# Revit family: Haworth_Circa_Pendant
name_source: partatom
category: Lighting Fixtures
revit_build: Autodesk Revit 2018 (Build: 20170223_1515(x64)
units: mm (PartAtom-declared; Revit-internal decimal feet)

## family parameters
Always vertical = Yes
Cut with Voids When Loaded = No
Host = Ceiling
Light Source = Yes
OmniClass Number = 23.80.70.11
OmniClass Title = Luminaries for Internal Lighting
Part Type = Normal
Room Calculation Point = No
Round Connector Dimension = Use Diameter
Shared = No

## types (2) — shared parameters
Apparent Load = 0 VA
Assembly Code = D5020200
Color Filter = 16777215
Cords Finish = Haworth _ Metal _ Satin Aluminum_Grey-Cord TR-E05
Dimming Lamp Color Temperature Shift = <None>
Emit Shape Visible in Rendering = No
Emit from Circle Diameter = 1' - 6"
Glass Finish = Haworth _ Glass _ Frosted
Manufacturer = Haworth
Max. Cords Length = 10' - 0"
Min. Cords Length = 0' - 6"
Model = LRP1
Photometric Web File = generic
Revision Number = 1
Size = Verify Final Dim. w/ Haworth
URL = http://www.haworth.com
URL - Product = https://www.haworth.com
Warranty = http://www.haworth.com

## per-type parameters (varying)
| type | Description | Lamps Depth | Lamps Radius | Lamps Width | Large | Small | Tilt Angle |
| LRP1-1610 - Large | Haworth - Circa Pendant Light Large | 1' - 4" | 0' - 8" | 1' - 4" | Yes | No | 90.00° |
| LRP1-1210 - Small | Haworth Circa Pendant Light - Small | 1' - 0" | 0' - 6" | 1' - 0" | No | Yes | 60.00° |

## geometry (parser evidence)
native form markers: Sweep x2
no freeform markers — native parametric forms only
